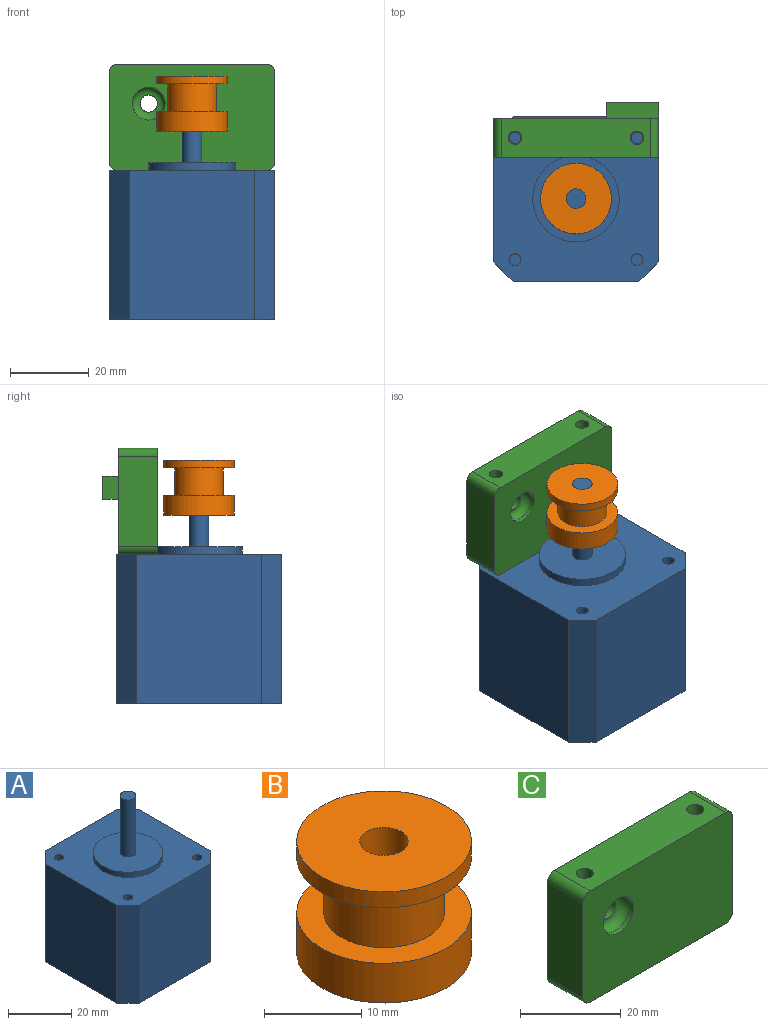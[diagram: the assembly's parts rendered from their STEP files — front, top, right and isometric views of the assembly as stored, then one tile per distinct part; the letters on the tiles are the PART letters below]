
ASSEMBLY  parts=3 mates=1
PART A: 22 faces, bbox 42x42x62 mm
  f0: plane 38x32mm, normal (-1,0,0), area 1216mm2, adj f4,f5,f8,f9
  f1: plane 38x32mm, normal (0,-1,0), area 1216mm2, adj f4,f5,f7,f9
  f2: plane 38x32mm, normal (1,0,0), area 1216mm2, adj f4,f5,f6,f7
  f3: plane 38x32mm, normal (0,1,0), area 1216mm2, adj f4,f5,f6,f8
  f4: plane 42x42mm, normal (0,0,1), area 1305.6mm2, adj f0,f1,f2,f3,f6,f7,f8,f9
  f5: plane 42x42mm, normal (0,0,-1), area 1714mm2, adj f0,f1,f2,f3,f6,f7,f8,f9
  f6: plane 38x5mm, normal (0.71,0.71,0), area 268.7mm2, adj f2,f3,f4,f5
  f7: plane 38x5mm, normal (0.71,-0.71,0), area 268.7mm2, adj f1,f2,f4,f5
  f8: plane 38x5mm, normal (-0.71,0.71,0), area 268.7mm2, adj f0,f3,f4,f5
  f9: plane 38x5mm, normal (-0.71,-0.71,0), area 268.7mm2, adj f0,f1,f4,f5
  f10: cylinder r=11mm len=22mm, axis (0,0,-1), area 138.2mm2, adj f4,f11
  f11: plane 22x22mm, normal (0,0,1), area 360.5mm2, adj f10,f12
  f12: cylinder r=2.5mm len=22mm, axis (0,0,-1), area 345.6mm2, adj f11,f13
  f13: plane 5x5mm, normal (0,0,1), area 19.6mm2, adj f12
  f14: cylinder r=1.5mm len=25mm, axis (0,0,1), area 235.6mm2, adj f4,f15
  f15: plane 3x3mm, normal (0,0,1), area 7.1mm2, adj f14
  f16: cylinder r=1.5mm len=25mm, axis (0,0,1), area 235.6mm2, adj f4,f17
  f17: plane 3x3mm, normal (0,0,1), area 7.1mm2, adj f16
  f18: cylinder r=1.5mm len=25mm, axis (0,0,1), area 235.6mm2, adj f4,f19
  f19: plane 3x3mm, normal (0,0,1), area 7.1mm2, adj f18
  f20: cylinder r=1.5mm len=25mm, axis (0,0,1), area 235.6mm2, adj f4,f21
  f21: plane 3x3mm, normal (0,0,1), area 7.1mm2, adj f20
PART B: 8 faces, bbox 18x18x14 mm
  f0: cylinder r=9mm len=18mm, axis (0,0,-1), area 282.7mm2, adj f1,f2
  f1: plane 18x18mm, normal (0,0,1), area 133.7mm2, adj f0,f3
  f2: plane 18x18mm, normal (0,0,-1), area 234.8mm2, adj f0,f7
  f3: cylinder r=6.2mm len=12.4mm, axis (0,0,-1), area 272.7mm2, adj f1,f6
  f4: cylinder r=9mm len=18mm, axis (0,0,-1), area 113.1mm2, adj f5,f6
  f5: plane 18x18mm, normal (0,0,1), area 234.8mm2, adj f4,f7
  f6: plane 18x18mm, normal (0,0,-1), area 133.7mm2, adj f3,f4
  f7: cylinder r=2.5mm len=14mm, axis (0,0,1), area 219.9mm2, adj f2,f5
PART C: 19 faces, bbox 42x14.4x27 mm
  f0: cylinder r=2.2mm len=7mm, axis (0,1,0), area 96.8mm2, adj f1,f14
  f1: plane 42x27mm, normal (0,1,0), area 1036.8mm2, adj f0,f2,f4,f5,f6,f9,f10,f11
  f2: plane 23x10mm, normal (-1,0,0), area 230mm2, adj f1,f3,f15,f17
  f3: plane 42x27mm, normal (0,-1,0), area 1075.1mm2, adj f2,f4,f5,f6,f13,f15,f16,f17
  f4: plane 23x14mm, normal (1,0,0), area 253.6mm2, adj f1,f3,f9,f11,f12,f16,f18
  f5: plane 38x10mm, normal (0,0,1), area 361.8mm2, adj f1,f3,f7,f8,f17,f18
  f6: plane 38x10mm, normal (0,0,-1), area 361.8mm2, adj f1,f3,f7,f8,f15,f16
  f7: cylinder r=1.7mm len=27mm, axis (0,0,1), area 288.4mm2, adj f5,f6
  f8: cylinder r=1.7mm len=27mm, axis (0,0,1), area 288.4mm2, adj f5,f6
  f9: plane 13.31x4mm, normal (0,0,-1), area 53.3mm2, adj f1,f4,f10,f12
  f10: plane 5.9x4mm, normal (-1,0,0), area 23.6mm2, adj f1,f9,f11,f12
  f11: plane 13.31x4mm, normal (0,0,1), area 53.3mm2, adj f1,f4,f10,f12
  f12: plane 13.31x5.9mm, normal (0,1,0), area 78.6mm2, adj f4,f9,f10,f11
  f13: cylinder r=4.2mm len=8.4mm, axis (0,-1,0), area 26.4mm2, adj f3,f14
  f14: torus R=2.2mm, axis (0,-1,0), area 68.6mm2, adj f0,f13
  f15: cylinder r=2mm len=10mm, axis (0,-1,0), area 31.4mm2, adj f1,f2,f3,f6
  f16: cylinder r=2mm len=10mm, axis (0,1,0), area 31.4mm2, adj f1,f3,f4,f6
  f17: cylinder r=2mm len=10mm, axis (0,1,0), area 31.4mm2, adj f1,f2,f3,f5
  f18: cylinder r=2mm len=10mm, axis (0,-1,0), area 31.4mm2, adj f1,f3,f4,f5
PLACE A t=(-19.22,-27.33,-36.28)mm
PLACE B t=(1.78,-6.33,11.72)mm
PLACE C t=(-2.36,4.17,1.72)mm
MATE fastened B.f0 <-> A.f10  axis (0,0,1) through (1.78,-6.33,25.72)mm
